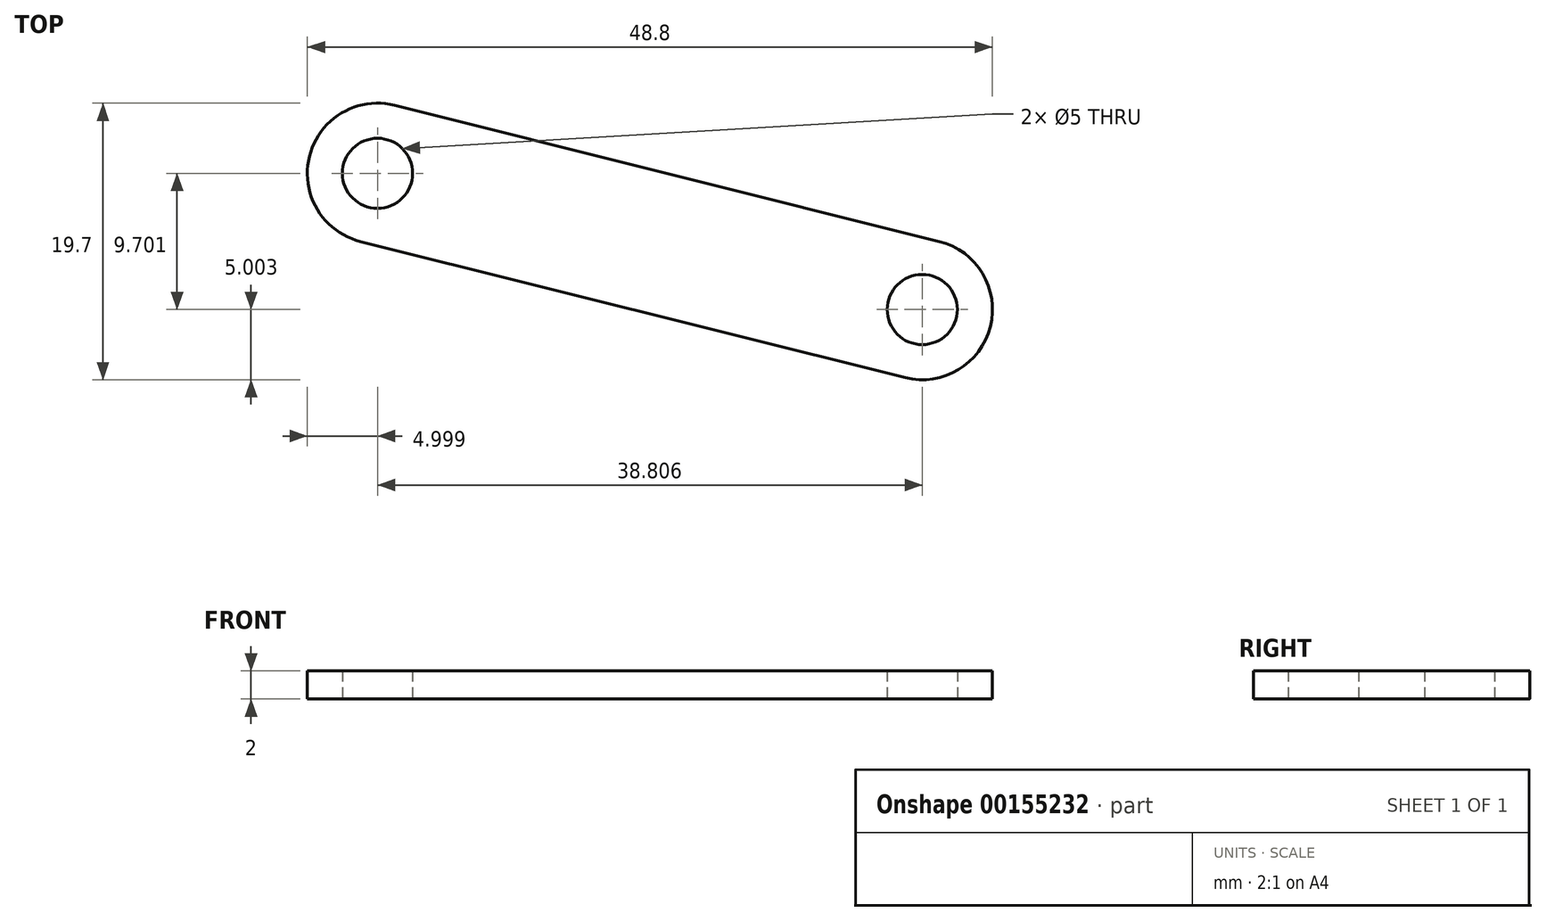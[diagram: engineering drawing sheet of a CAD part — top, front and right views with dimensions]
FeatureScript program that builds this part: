
annotation { "Feature Type Name" : "Feature", "Feature Type Description" : "" }
export const myFeature = defineFeature(function(context is Context, id is Id, definition is map)
    precondition{}
    {
        {
            var Q0;
            Q0=qCreatedBy(makeId("Top.planeOp"),FACE);
            var sketch = newSketch(context, id + "F0", { "sketchPlane" : qUnion([Q0])});
            skArc(sketch, "E0", {"start": v(-31.44, 40.17) * mm, "mid": v(-25.37, 43.81) * mm, "end": v(-29.01, 49.87) * mm});
            skArc(sketch, "E1", {"start": v(-67.82, 59.58) * mm, "mid": v(-73.88, 55.94) * mm, "end": v(-70.24, 49.87) * mm});
            skLineSegment(sketch, "E2", {"start": v(-67.82, 59.58) * mm, "end": v(-29.01, 49.87) * mm});
            skLineSegment(sketch, "E3", {"start": v(-70.24, 49.87) * mm, "end": v(-31.44, 40.17) * mm});
            skCircle(sketch, "E4", {"center": v(-69.03, 54.72) * mm, "radius": 2.5 * mm});
            skCircle(sketch, "E5", {"center": v(-30.23, 45.02) * mm, "radius": 2.5 * mm});
            skSolve(sketch);
        }
        {
            var Q0;
            Q0 = qSketchRegion(id + "F0", true);
            extrude(context, id + "F1", {"entities" : qUnion([Q0]), "depth" : 2 * mm});
        }
    });
